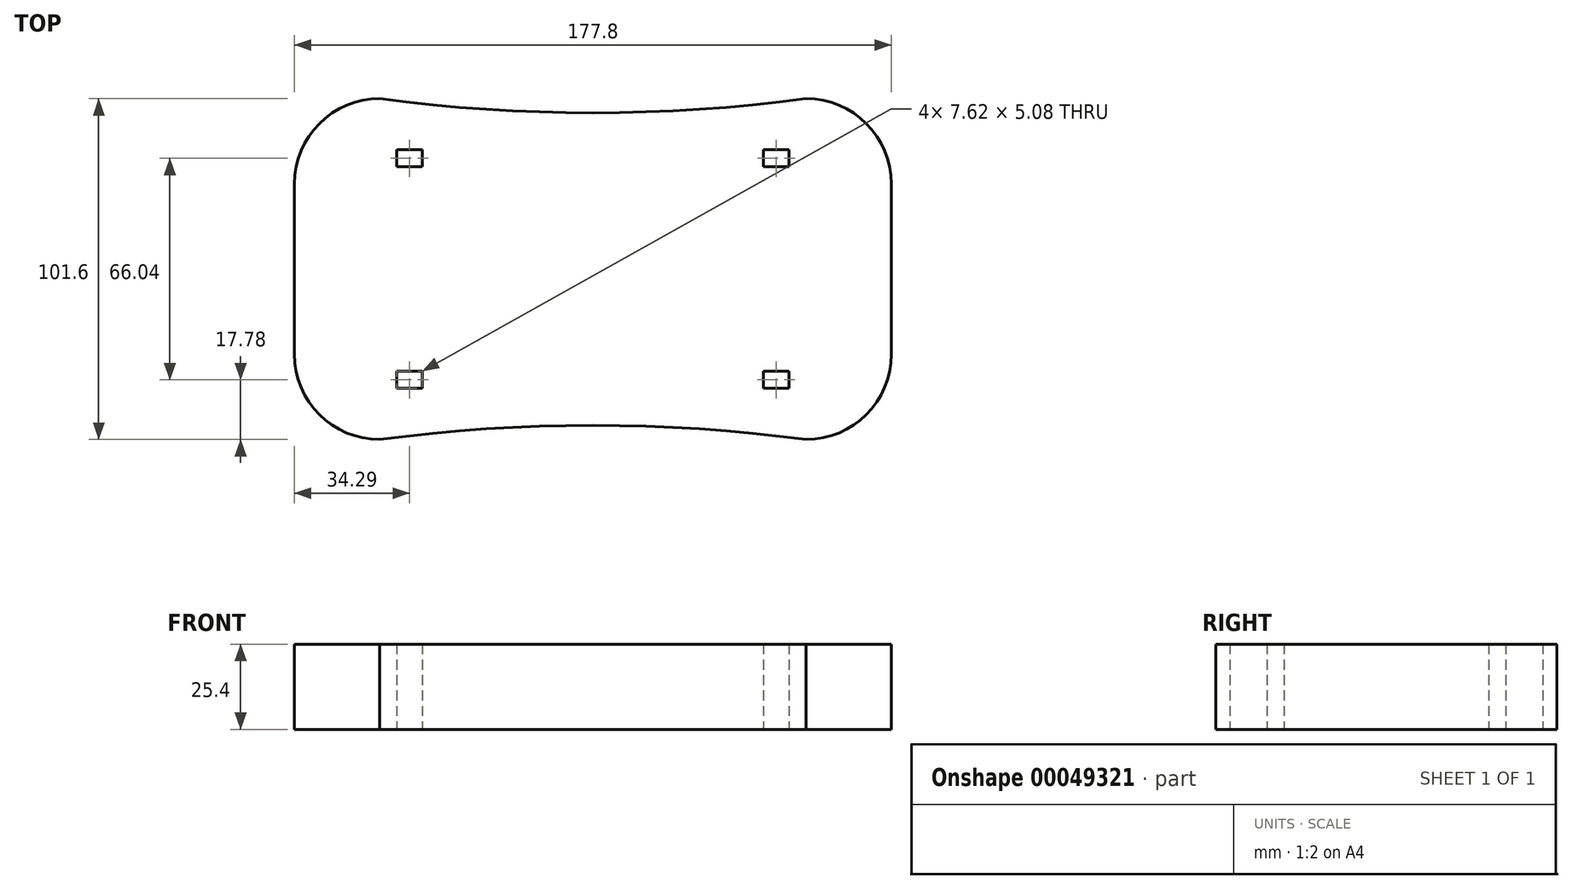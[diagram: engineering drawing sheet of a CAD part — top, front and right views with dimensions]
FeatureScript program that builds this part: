
annotation { "Feature Type Name" : "Feature", "Feature Type Description" : "" }
export const myFeature = defineFeature(function(context is Context, id is Id, definition is map)
    precondition{}
    {
        {
            var Q0;
            Q0=qCreatedBy(makeId("Top.planeOp"),FACE);
            var sketch = newSketch(context, id + "F0", { "sketchPlane" : qUnion([Q0])});
            skLineSegment(sketch, "E0.rect.left", {"start": v(88.9, -25.4) * mm, "end": v(88.9, 25.4) * mm});
            skLineSegment(sketch, "E0.rect.right", {"start": v(-88.9, -25.4) * mm, "end": v(-88.9, 25.4) * mm});
            skPoint(sketch, "E0.rect.middle", {"position": v(0, 0) * mm});
            skPoint(sketch, "E1.visualSharp", {"position": v(-88.9, 50.8) * mm});
            skArc(sketch, "E1.filletArc", {"start": v(-63.5, 50.8) * mm, "mid": v(-81.46, 43.36) * mm, "end": v(-88.9, 25.4) * mm});
            skPoint(sketch, "E2.visualSharp", {"position": v(-88.9, -50.8) * mm});
            skArc(sketch, "E2.filletArc", {"start": v(-88.9, -25.4) * mm, "mid": v(-81.46, -43.36) * mm, "end": v(-63.5, -50.8) * mm});
            skPoint(sketch, "E3.visualSharp", {"position": v(88.9, -50.8) * mm});
            skArc(sketch, "E3.filletArc", {"start": v(63.5, -50.8) * mm, "mid": v(81.46, -43.36) * mm, "end": v(88.9, -25.4) * mm});
            skPoint(sketch, "E4.visualSharp", {"position": v(88.9, 50.8) * mm});
            skArc(sketch, "E4.filletArc", {"start": v(88.9, 25.4) * mm, "mid": v(81.46, 43.36) * mm, "end": v(63.5, 50.8) * mm});
            skArc(sketch, "E5", {"start": v(-63.5, 50.8) * mm, "mid": v(0, 46.58) * mm, "end": v(63.5, 50.8) * mm});
            skPoint(sketch, "E5.third.point", {"position": v(0, 46.58) * mm});
            skArc(sketch, "E6.MirrorCS", {"start": v(-63.5, -50.8) * mm, "mid": v(0, -46.58) * mm, "end": v(63.5, -50.8) * mm});
            skLineSegment(sketch, "E7.bottom", {"start": v(-58.42, 35.56) * mm, "end": v(-50.8, 35.56) * mm});
            skLineSegment(sketch, "E7.top", {"start": v(-58.42, 30.48) * mm, "end": v(-50.8, 30.48) * mm});
            skLineSegment(sketch, "E7.left", {"start": v(-58.42, 35.56) * mm, "end": v(-58.42, 30.48) * mm});
            skLineSegment(sketch, "E7.right", {"start": v(-50.8, 35.56) * mm, "end": v(-50.8, 30.48) * mm});
            skLineSegment(sketch, "E8.MirrorCS", {"start": v(-50.8, -35.56) * mm, "end": v(-50.8, -30.48) * mm});
            skLineSegment(sketch, "E9.MirrorCS", {"start": v(-58.42, -35.56) * mm, "end": v(-58.42, -30.48) * mm});
            skLineSegment(sketch, "E10.MirrorCS", {"start": v(-58.42, -30.48) * mm, "end": v(-50.8, -30.48) * mm});
            skLineSegment(sketch, "E11.MirrorCS", {"start": v(-58.42, -35.56) * mm, "end": v(-50.8, -35.56) * mm});
            skLineSegment(sketch, "E12.MirrorCS", {"start": v(50.8, -35.56) * mm, "end": v(50.8, -30.48) * mm});
            skLineSegment(sketch, "E13.MirrorCS", {"start": v(50.8, 35.56) * mm, "end": v(50.8, 30.48) * mm});
            skLineSegment(sketch, "E14.MirrorCS", {"start": v(58.42, 35.56) * mm, "end": v(58.42, 30.48) * mm});
            skLineSegment(sketch, "E15.MirrorCS", {"start": v(58.42, -35.56) * mm, "end": v(58.42, -30.48) * mm});
            skLineSegment(sketch, "E16.MirrorCS", {"start": v(58.42, 30.48) * mm, "end": v(50.8, 30.48) * mm});
            skLineSegment(sketch, "E17.MirrorCS", {"start": v(58.42, -30.48) * mm, "end": v(50.8, -30.48) * mm});
            skLineSegment(sketch, "E18.MirrorCS", {"start": v(58.42, 35.56) * mm, "end": v(50.8, 35.56) * mm});
            skLineSegment(sketch, "E19.MirrorCS", {"start": v(58.42, -35.56) * mm, "end": v(50.8, -35.56) * mm});
            skSolve(sketch);
        }
        {
            var Q0;
            Q0 = qSketchRegion(id + "F0", true);
            extrude(context, id + "F1", {"entities" : qUnion([Q0]), "depth" : 25.4 * mm});
        }
    });
